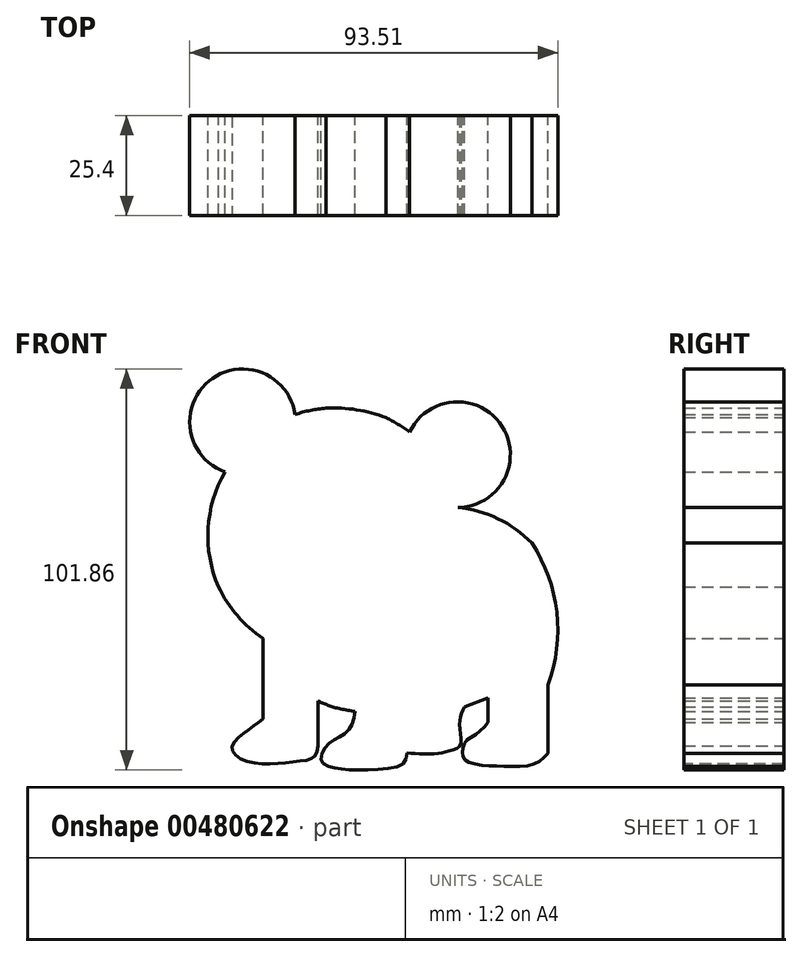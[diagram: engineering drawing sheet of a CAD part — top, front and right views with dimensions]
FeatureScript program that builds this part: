
annotation { "Feature Type Name" : "Feature", "Feature Type Description" : "" }
export const myFeature = defineFeature(function(context is Context, id is Id, definition is map)
    precondition{}
    {
        {
            var Q0;
            Q0=qCreatedBy(makeId("Front.planeOp"),FACE);
            var sketch = newSketch(context, id + "F0", { "sketchPlane" : qUnion([Q0])});
            skArc(sketch, "E0", {"start": v(-15.23, 45.4) * mm, "mid": v(-40.58, 29.73) * mm, "end": v(-42.57, 0) * mm});
            skArc(sketch, "E1", {"start": v(16.42, 0) * mm, "mid": v(16.85, 24.79) * mm, "end": v(0, 42.97) * mm});
            skArc(sketch, "E2", {"start": v(0, 42.97) * mm, "mid": v(-7.49, 45) * mm, "end": v(-15.23, 45.4) * mm});
            skArc(sketch, "E3", {"start": v(-42.57, 0) * mm, "mid": v(-36.63, -8.55) * mm, "end": v(-28.36, -14.88) * mm});
            skArc(sketch, "E4", {"start": v(-4.35, -17.6) * mm, "mid": v(8, -11.1) * mm, "end": v(16.42, 0) * mm});
            skArc(sketch, "E5", {"start": v(-28.36, -14.88) * mm, "mid": v(-17, -21.87) * mm, "end": v(-4.35, -17.6) * mm});
            skArc(sketch, "E6", {"start": v(-23.1, 43.8) * mm, "mid": v(-44.94, 52.3) * mm, "end": v(-40.9, 29.2) * mm});
            skArc(sketch, "E7", {"start": v(18.25, 20.15) * mm, "mid": v(29.47, 40.8) * mm, "end": v(6.01, 39.31) * mm});
            skLineSegment(sketch, "E8", {"start": v(-31.26, -13.1) * mm, "end": v(-31.26, -33.5) * mm});
            skLineSegment(sketch, "E9", {"start": v(-17.28, -29.02) * mm, "end": v(-17.28, -40.45) * mm});
            skFitSpline(sketch, "E10", {"points": [v(-17.28, -40.45) * mm, v(-18.23, -43.2) * mm, v(-21.85, -44.26) * mm, v(-28.52, -44.92) * mm, v(-35.57, -44.26) * mm, v(-39, -41.68) * mm, v(-38.33, -39.11) * mm, v(-34.71, -36.16) * mm, v(-31.26, -33.5) * mm], "startDerivative": vector(-4.53, -31.54) * mm, "endDerivative": vector(26.68, 21.35) * mm});
            skFitSpline(sketch, "E11", {"points": [v(-17.28, -29.02) * mm, v(-13.38, -30.54) * mm, v(-7.85, -31.68) * mm], "startDerivative": vector(8, -3.56) * mm, "endDerivative": vector(10.78, -1.82) * mm});
            skFitSpline(sketch, "E12", {"points": [v(-7.85, -31.68) * mm, v(-8.8, -35.2) * mm, v(-10.9, -37.59) * mm, v(-13.85, -39.3) * mm, v(-15.95, -41.59) * mm, v(-16.42, -44.35) * mm, v(-14.04, -45.78) * mm, v(-9.78, -46.45) * mm, v(-1.76, -46.35) * mm, v(4.34, -44.92) * mm, v(5.39, -42.16) * mm], "startDerivative": vector(-6.87, -38.56) * mm, "endDerivative": vector(4.78, 35.78) * mm});
            skFitSpline(sketch, "E13", {"points": [v(19.96, -30.44) * mm, v(18.91, -32.92) * mm, v(18.82, -36.45) * mm, v(18.82, -40.35) * mm, v(16.15, -41.59) * mm, v(13.3, -42.35) * mm, v(8.91, -42.45) * mm, v(5.39, -42.16) * mm], "startDerivative": vector(-9.72, -18.67) * mm, "endDerivative": vector(-22.97, 2.22) * mm});
            skFitSpline(sketch, "E14", {"points": [v(19.96, -30.44) * mm, v(25.96, -28.25) * mm], "startDerivative": vector(6, 2.2) * mm, "endDerivative": vector(6, 2.2) * mm});
            skLineSegment(sketch, "E15", {"start": v(25.96, -28.25) * mm, "end": v(25.96, -34.45) * mm});
            skFitSpline(sketch, "E16", {"points": [v(25.96, -34.45) * mm, v(22.91, -37.4) * mm, v(20.24, -39.3) * mm, v(19.48, -41.78) * mm, v(19.77, -43.68) * mm, v(23.48, -45.2) * mm, v(30.44, -45.59) * mm, v(37.58, -45.02) * mm, v(41.2, -42.26) * mm], "startDerivative": vector(-23, -25.83) * mm, "endDerivative": vector(23.94, 25.13) * mm});
            skLineSegment(sketch, "E17", {"start": v(41.2, -42.26) * mm, "end": v(41.2, -24.92) * mm});
            skArc(sketch, "E18", {"start": v(41.2, -24.92) * mm, "mid": v(43.37, -6.43) * mm, "end": v(37.06, 11.1) * mm});
            skArc(sketch, "E19", {"start": v(37.06, 11.1) * mm, "mid": v(28.46, 17.3) * mm, "end": v(18.25, 20.15) * mm});
            skSolve(sketch);
        }
        {
            var Q0;
            Q0 = qSketchRegion(id + "F0", true);
            extrude(context, id + "F1", {"entities" : qUnion([Q0]), "depth" : 25.4 * mm});
        }
    });
